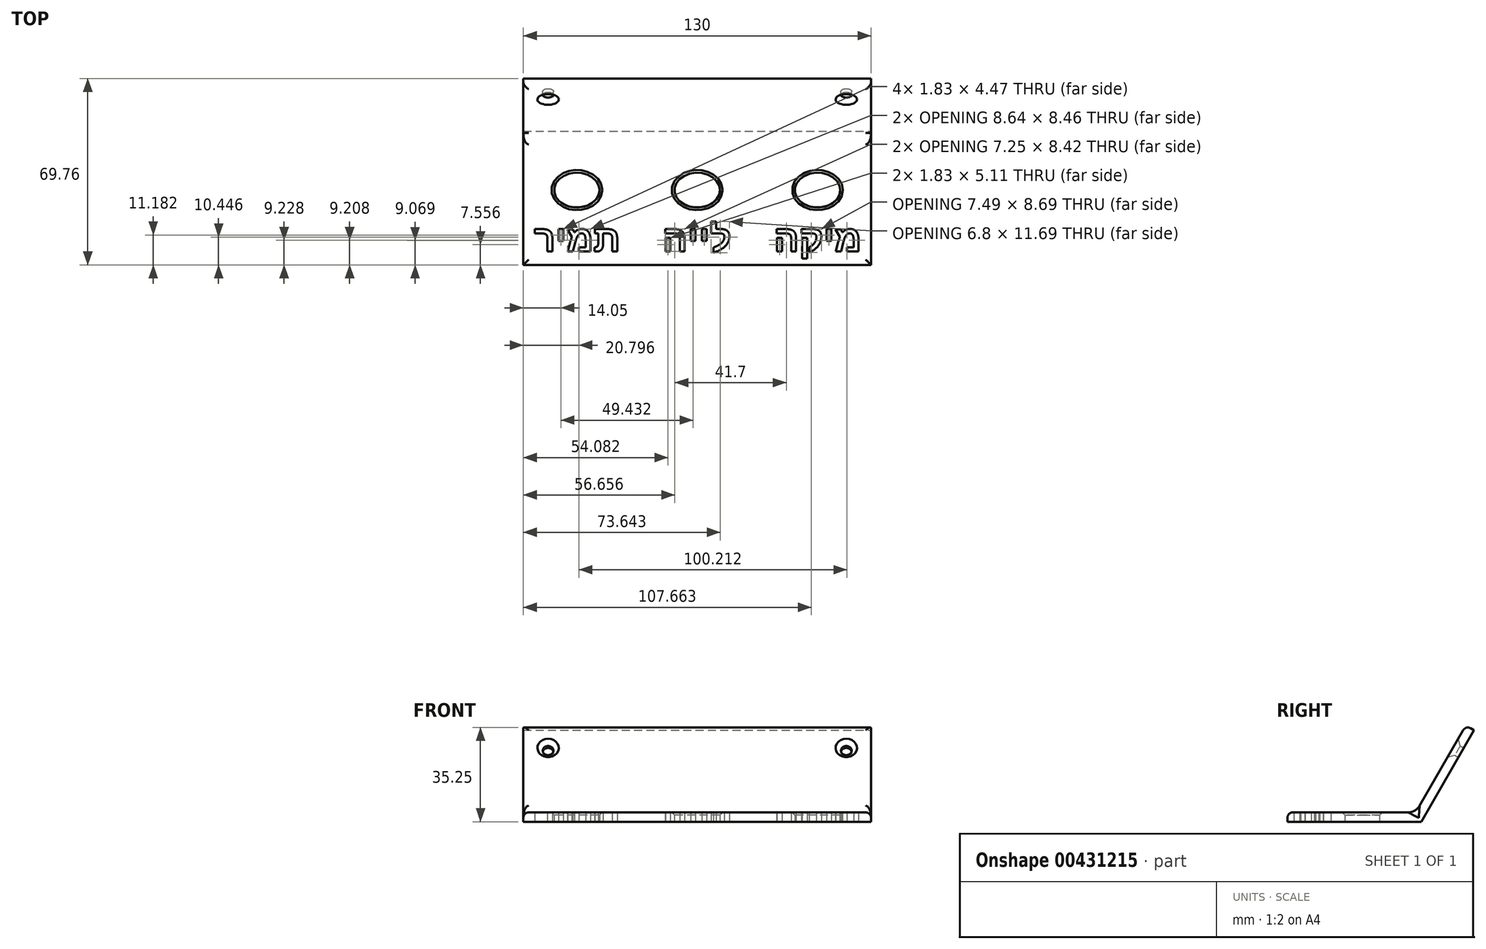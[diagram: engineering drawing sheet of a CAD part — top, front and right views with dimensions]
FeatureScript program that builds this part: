
annotation { "Feature Type Name" : "Feature", "Feature Type Description" : "" }
export const myFeature = defineFeature(function(context is Context, id is Id, definition is map)
    precondition{}
    {
        {
            var Q0;
            Q0=qCreatedBy(makeId("Top.planeOp"),FACE);
            var sketch = newSketch(context, id + "F0", { "sketchPlane" : qUnion([Q0])});
            skLineSegment(sketch, "E0.bottom", {"start": v(-65, 0) * mm, "end": v(65, 0) * mm});
            skLineSegment(sketch, "E0.top", {"start": v(-65, -50) * mm, "end": v(65, -50) * mm});
            skLineSegment(sketch, "E0.left", {"start": v(-65, 0) * mm, "end": v(-65, -50) * mm});
            skLineSegment(sketch, "E0.right", {"start": v(65, 0) * mm, "end": v(65, -50) * mm});
            skText(sketch, "E1", { "text": "רימת", "fontName": "Arimo-Bold.ttf"});
            skText(sketch, "E2", { "text": "הייל", "fontName": "Arimo-Bold.ttf"});
            skText(sketch, "E3", { "text": "הקימ", "fontName": "Arimo-Bold.ttf"});
            skLineSegment(sketch, "E4", {"start": v(0, 0) * mm, "end": v(0, -45) * mm});
            skLineSegment(sketch, "E5", {"start": v(-65, -22) * mm, "end": v(65, -22) * mm, "construction": true});
            skPoint(sketch, "E6", {"position": v(0, 0) * mm});
            skLineSegment(sketch, "E7", {"start": v(-65, -45) * mm, "end": v(65, -45) * mm, "construction": true});
            skEllipse(sketch, "E8", {"center": v(-45, -22) * mm, "majorRadius": 8.5 * mm, "minorRadius": 6.5 * mm, "majorAxis": v(1, 0)});
            skEllipse(sketch, "E9", {"center": v(45, -22) * mm, "majorRadius": 8.5 * mm, "minorRadius": 6.5 * mm, "majorAxis": v(1, 0)});
            skEllipse(sketch, "E10", {"center": v(0, -22) * mm, "majorRadius": 8.5 * mm, "minorRadius": 6.5 * mm, "majorAxis": v(1, 0)});
            const initialGuessF0  = {"E1": [-0.06105, -0.045, 1, 0, 0.01], "E2": [-0.013, -0.045, 1, 0, 0.01], "E3": [0.0287, -0.045, 1, 0, 0.01]};
            skSetInitialGuess(sketch, initialGuessF0);
            skSolve(sketch);
        }
        {
            var Q0;
            Q0=makeQuery(id+"F0.imprint","IMPRINT",FACE,{"disambiguationData":[TD([[makeQuery(id+"F0.imprint","IMPRINT",EDGE,{"derivedFrom":sQuery(id+"F0.wireOp",EDGE,"E0.bottom")}),-1.0]])]});
            extrude(context, id + "F1", {"entities" : qUnion([Q0]), "depth" : 3.5 * mm});
        }
        {
            var Q0;
            Q0=makeQuery(id+"F1.opExtrude","CAP_EDGE",EDGE,{"disambiguationData":[OSD([sQuery(id+"F0.wireOp",EDGE,"E8")])],"isStart":false});
            var Q1;
            Q1=makeQuery(id+"F1.opExtrude","CAP_EDGE",EDGE,{"disambiguationData":[OSD([sQuery(id+"F0.wireOp",EDGE,"E10")])],"isStart":false});
            var Q2;
            Q2=makeQuery(id+"F1.opExtrude","CAP_EDGE",EDGE,{"disambiguationData":[OSD([sQuery(id+"F0.wireOp",EDGE,"E9")])],"isStart":false});
            chamfer(context, id + "F2", {"entities" : qUnion([Q0, Q1, Q2]), "width" : 1 * mm, "tangentPropagation" : true});
        }
        {
            var Q0;
            Q0=makeQuery(id+"F1.opExtrude","CAP_EDGE",EDGE,{"disambiguationData":[OSD([sQuery(id+"F0.wireOp",EDGE,"E0.bottom")])],"isStart":true});
            cPlane(context, id + "F3", {"entities" : qUnion([Q0]), "cplaneType" : CPlaneType.LINE_ANGLE, "offset" : 25 * mm, "angle" : 330 * degree, "width" : 150 * mm, "height" : 150 * mm});
        }
        {
            var Q0;
            Q0=qCreatedBy(id+"F3.planeOp",FACE);
            var sketch = newSketch(context, id + "F4", { "sketchPlane" : qUnion([Q0])});
            skLineSegment(sketch, "E11.bottom", {"start": v(65, 0) * mm, "end": v(-65, 0) * mm});
            skLineSegment(sketch, "E11.top", {"start": v(65, 0) * mm, "end": v(-65, 0) * mm});
            skLineSegment(sketch, "E11.left", {"start": v(65, 0) * mm, "end": v(65, 0) * mm});
            skLineSegment(sketch, "E11.right", {"start": v(-65, 0) * mm, "end": v(-65, 0) * mm});
            skLineSegment(sketch, "E12.bottom", {"start": v(65, 39.53) * mm, "end": v(-65, 39.53) * mm});
            skLineSegment(sketch, "E12.left", {"start": v(65, 39.53) * mm, "end": v(65, 0) * mm});
            skLineSegment(sketch, "E12.right", {"start": v(-65, 39.53) * mm, "end": v(-65, 0) * mm});
            skPoint(sketch, "E13", {"position": v(0, 0) * mm});
            skPoint(sketch, "E14", {"position": v(0, 39.53) * mm});
            skLineSegment(sketch, "E15", {"start": v(0, 39.53) * mm, "end": v(0, 0) * mm, "construction": true});
            skCircle(sketch, "E16", {"center": v(-55.75, 29.86) * mm, "radius": 2 * mm});
            skCircle(sketch, "E17.MirrorC", {"center": v(55.75, 29.86) * mm, "radius": 2 * mm});
            skSolve(sketch);
        }
        {
            var Q0;
            Q0 = qSketchRegion(id + "F4", true);
            extrude(context, id + "F5", {"entities" : qUnion([Q0]), "operationType" : NewBodyOperationType.ADD, "oppositeDirection" : true, "depth" : 3.5 * mm});
        }
        {
            var Q0;
            Q0=makeQuery(id+"F1.opExtrude","CAP_EDGE",EDGE,{"disambiguationData":[OSD([sQuery(id+"F0.wireOp",EDGE,"E0.left")])],"isStart":false});
            var Q1;
            Q1=makeQuery(id+"F1.opExtrude","CAP_EDGE",EDGE,{"disambiguationData":[OSD([sQuery(id+"F0.wireOp",EDGE,"E0.top")])],"isStart":false});
            var Q2;
            Q2=makeQuery(id+"F1.opExtrude","CAP_EDGE",EDGE,{"disambiguationData":[OSD([sQuery(id+"F0.wireOp",EDGE,"E0.right")])],"isStart":false});
            var Q3;
            {var subQ0=sQuery(id+"F4.wireOp",EDGE,"E12.left");var subQ1=sQuery(id+"F0.wireOp",EDGE,"E0.right");Q3=makeQuery(id+"FBdAfcJwTmfcVVD_1.opChamfer","BLEND_EDGE",EDGE,{"blendedFrom":[makeQuery(id+"F5.boolean.opBoolean","INTERSECT",EDGE,{"derivedFrom":[makeQuery(id+"F1.opExtrude","CAP_FACE",FACE,{"disambiguationData":[OSD([sQuery(id+"F0.wireOp",EDGE,"E0.bottom"),sQuery(id+"F0.wireOp",EDGE,"E0.top"),sQuery(id+"F0.wireOp",EDGE,"E0.left"),subQ1,sQuery(id+"F0.wireOp",EDGE,"E1.sketch_text.stroke-0"),sQuery(id+"F0.wireOp",EDGE,"E1.sketch_text.stroke-1"),sQuery(id+"F0.wireOp",EDGE,"E1.sketch_text.stroke-2"),sQuery(id+"F0.wireOp",EDGE,"E1.sketch_text.stroke-3"),sQuery(id+"F0.wireOp",EDGE,"E1.sketch_text.stroke-4"),sQuery(id+"F0.wireOp",EDGE,"E1.sketch_text.stroke-5"),sQuery(id+"F0.wireOp",EDGE,"E1.sketch_text.stroke-6"),sQuery(id+"F0.wireOp",EDGE,"E1.sketch_text.stroke-7"),sQuery(id+"F0.wireOp",EDGE,"E1.sketch_text.stroke-8"),sQuery(id+"F0.wireOp",EDGE,"E1.sketch_text.stroke-9"),sQuery(id+"F0.wireOp",EDGE,"E1.sketch_text.stroke-10"),sQuery(id+"F0.wireOp",EDGE,"E1.sketch_text.stroke-11"),sQuery(id+"F0.wireOp",EDGE,"E1.sketch_text.stroke-12"),sQuery(id+"F0.wireOp",EDGE,"E1.sketch_text.stroke-13"),sQuery(id+"F0.wireOp",EDGE,"E1.sketch_text.stroke-14"),sQuery(id+"F0.wireOp",EDGE,"E1.sketch_text.stroke-15"),sQuery(id+"F0.wireOp",EDGE,"E1.sketch_text.stroke-16"),sQuery(id+"F0.wireOp",EDGE,"E1.sketch_text.stroke-17"),sQuery(id+"F0.wireOp",EDGE,"E1.sketch_text.stroke-18"),sQuery(id+"F0.wireOp",EDGE,"E1.sketch_text.stroke-19"),sQuery(id+"F0.wireOp",EDGE,"E1.sketch_text.stroke-20"),sQuery(id+"F0.wireOp",EDGE,"E1.sketch_text.stroke-21"),sQuery(id+"F0.wireOp",EDGE,"E1.sketch_text.stroke-22"),sQuery(id+"F0.wireOp",EDGE,"E1.sketch_text.stroke-23"),sQuery(id+"F0.wireOp",EDGE,"E1.sketch_text.stroke-24"),sQuery(id+"F0.wireOp",EDGE,"E1.sketch_text.stroke-25"),sQuery(id+"F0.wireOp",EDGE,"E1.sketch_text.stroke-26"),sQuery(id+"F0.wireOp",EDGE,"E1.sketch_text.stroke-27"),sQuery(id+"F0.wireOp",EDGE,"E1.sketch_text.stroke-28"),sQuery(id+"F0.wireOp",EDGE,"E1.sketch_text.stroke-29"),sQuery(id+"F0.wireOp",EDGE,"E1.sketch_text.stroke-30"),sQuery(id+"F0.wireOp",EDGE,"E1.sketch_text.stroke-31"),sQuery(id+"F0.wireOp",EDGE,"E1.sketch_text.stroke-32"),sQuery(id+"F0.wireOp",EDGE,"E1.sketch_text.stroke-33"),sQuery(id+"F0.wireOp",EDGE,"E1.sketch_text.stroke-34"),sQuery(id+"F0.wireOp",EDGE,"E1.sketch_text.stroke-35"),sQuery(id+"F0.wireOp",EDGE,"E1.sketch_text.stroke-36"),sQuery(id+"F0.wireOp",EDGE,"E1.sketch_text.stroke-37"),sQuery(id+"F0.wireOp",EDGE,"E1.sketch_text.stroke-38"),sQuery(id+"F0.wireOp",EDGE,"E1.sketch_text.stroke-39"),sQuery(id+"F0.wireOp",EDGE,"E1.sketch_text.stroke-40"),sQuery(id+"F0.wireOp",EDGE,"E1.sketch_text.stroke-41"),sQuery(id+"F0.wireOp",EDGE,"E1.sketch_text.stroke-42"),sQuery(id+"F0.wireOp",EDGE,"E1.sketch_text.stroke-43"),sQuery(id+"F0.wireOp",EDGE,"E1.sketch_text.stroke-44"),sQuery(id+"F0.wireOp",EDGE,"E1.sketch_text.stroke-45"),sQuery(id+"F0.wireOp",EDGE,"E1.sketch_text.stroke-46"),sQuery(id+"F0.wireOp",EDGE,"E1.sketch_text.stroke-47"),sQuery(id+"F0.wireOp",EDGE,"E1.sketch_text.stroke-48"),sQuery(id+"F0.wireOp",EDGE,"E1.sketch_text.stroke-49"),sQuery(id+"F0.wireOp",EDGE,"E1.sketch_text.stroke-50"),sQuery(id+"F0.wireOp",EDGE,"E1.sketch_text.stroke-51"),sQuery(id+"F0.wireOp",EDGE,"E1.sketch_text.stroke-52"),sQuery(id+"F0.wireOp",EDGE,"E1.sketch_text.stroke-53"),sQuery(id+"F0.wireOp",EDGE,"E1.sketch_text.stroke-54"),sQuery(id+"F0.wireOp",EDGE,"E1.sketch_text.stroke-55"),sQuery(id+"F0.wireOp",EDGE,"E2.sketch_text.stroke-0"),sQuery(id+"F0.wireOp",EDGE,"E2.sketch_text.stroke-1"),sQuery(id+"F0.wireOp",EDGE,"E2.sketch_text.stroke-2"),sQuery(id+"F0.wireOp",EDGE,"E2.sketch_text.stroke-3"),sQuery(id+"F0.wireOp",EDGE,"E2.sketch_text.stroke-4"),sQuery(id+"F0.wireOp",EDGE,"E2.sketch_text.stroke-5"),sQuery(id+"F0.wireOp",EDGE,"E2.sketch_text.stroke-6"),sQuery(id+"F0.wireOp",EDGE,"E2.sketch_text.stroke-7"),sQuery(id+"F0.wireOp",EDGE,"E2.sketch_text.stroke-8"),sQuery(id+"F0.wireOp",EDGE,"E2.sketch_text.stroke-9"),sQuery(id+"F0.wireOp",EDGE,"E2.sketch_text.stroke-10"),sQuery(id+"F0.wireOp",EDGE,"E2.sketch_text.stroke-11"),sQuery(id+"F0.wireOp",EDGE,"E2.sketch_text.stroke-12"),sQuery(id+"F0.wireOp",EDGE,"E2.sketch_text.stroke-13"),sQuery(id+"F0.wireOp",EDGE,"E2.sketch_text.stroke-14"),sQuery(id+"F0.wireOp",EDGE,"E2.sketch_text.stroke-15"),sQuery(id+"F0.wireOp",EDGE,"E2.sketch_text.stroke-16"),sQuery(id+"F0.wireOp",EDGE,"E2.sketch_text.stroke-17"),sQuery(id+"F0.wireOp",EDGE,"E2.sketch_text.stroke-18"),sQuery(id+"F0.wireOp",EDGE,"E2.sketch_text.stroke-19"),sQuery(id+"F0.wireOp",EDGE,"E2.sketch_text.stroke-20"),sQuery(id+"F0.wireOp",EDGE,"E2.sketch_text.stroke-21"),sQuery(id+"F0.wireOp",EDGE,"E2.sketch_text.stroke-22"),sQuery(id+"F0.wireOp",EDGE,"E2.sketch_text.stroke-23"),sQuery(id+"F0.wireOp",EDGE,"E2.sketch_text.stroke-24"),sQuery(id+"F0.wireOp",EDGE,"E2.sketch_text.stroke-25"),sQuery(id+"F0.wireOp",EDGE,"E2.sketch_text.stroke-26"),sQuery(id+"F0.wireOp",EDGE,"E2.sketch_text.stroke-27"),sQuery(id+"F0.wireOp",EDGE,"E2.sketch_text.stroke-28"),sQuery(id+"F0.wireOp",EDGE,"E2.sketch_text.stroke-29"),sQuery(id+"F0.wireOp",EDGE,"E2.sketch_text.stroke-30"),sQuery(id+"F0.wireOp",EDGE,"E2.sketch_text.stroke-31"),sQuery(id+"F0.wireOp",EDGE,"E2.sketch_text.stroke-32"),sQuery(id+"F0.wireOp",EDGE,"E2.sketch_text.stroke-33"),sQuery(id+"F0.wireOp",EDGE,"E3.sketch_text.stroke-0"),sQuery(id+"F0.wireOp",EDGE,"E3.sketch_text.stroke-1"),sQuery(id+"F0.wireOp",EDGE,"E3.sketch_text.stroke-2"),sQuery(id+"F0.wireOp",EDGE,"E3.sketch_text.stroke-3"),sQuery(id+"F0.wireOp",EDGE,"E3.sketch_text.stroke-4"),sQuery(id+"F0.wireOp",EDGE,"E3.sketch_text.stroke-5"),sQuery(id+"F0.wireOp",EDGE,"E3.sketch_text.stroke-6"),sQuery(id+"F0.wireOp",EDGE,"E3.sketch_text.stroke-7"),sQuery(id+"F0.wireOp",EDGE,"E3.sketch_text.stroke-8"),sQuery(id+"F0.wireOp",EDGE,"E3.sketch_text.stroke-9"),sQuery(id+"F0.wireOp",EDGE,"E3.sketch_text.stroke-10"),sQuery(id+"F0.wireOp",EDGE,"E3.sketch_text.stroke-11"),sQuery(id+"F0.wireOp",EDGE,"E3.sketch_text.stroke-12"),sQuery(id+"F0.wireOp",EDGE,"E3.sketch_text.stroke-13"),sQuery(id+"F0.wireOp",EDGE,"E3.sketch_text.stroke-14"),sQuery(id+"F0.wireOp",EDGE,"E3.sketch_text.stroke-15"),sQuery(id+"F0.wireOp",EDGE,"E3.sketch_text.stroke-16"),sQuery(id+"F0.wireOp",EDGE,"E3.sketch_text.stroke-17"),sQuery(id+"F0.wireOp",EDGE,"E3.sketch_text.stroke-18"),sQuery(id+"F0.wireOp",EDGE,"E3.sketch_text.stroke-19"),sQuery(id+"F0.wireOp",EDGE,"E3.sketch_text.stroke-20"),sQuery(id+"F0.wireOp",EDGE,"E3.sketch_text.stroke-21"),sQuery(id+"F0.wireOp",EDGE,"E3.sketch_text.stroke-22"),sQuery(id+"F0.wireOp",EDGE,"E3.sketch_text.stroke-23"),sQuery(id+"F0.wireOp",EDGE,"E3.sketch_text.stroke-24"),sQuery(id+"F0.wireOp",EDGE,"E3.sketch_text.stroke-25"),sQuery(id+"F0.wireOp",EDGE,"E3.sketch_text.stroke-26"),sQuery(id+"F0.wireOp",EDGE,"E3.sketch_text.stroke-27"),sQuery(id+"F0.wireOp",EDGE,"E3.sketch_text.stroke-28"),sQuery(id+"F0.wireOp",EDGE,"E3.sketch_text.stroke-29"),sQuery(id+"F0.wireOp",EDGE,"E3.sketch_text.stroke-30"),sQuery(id+"F0.wireOp",EDGE,"E3.sketch_text.stroke-31"),sQuery(id+"F0.wireOp",EDGE,"E3.sketch_text.stroke-32"),sQuery(id+"F0.wireOp",EDGE,"E3.sketch_text.stroke-33"),sQuery(id+"F0.wireOp",EDGE,"E3.sketch_text.stroke-34"),sQuery(id+"F0.wireOp",EDGE,"E3.sketch_text.stroke-35"),sQuery(id+"F0.wireOp",EDGE,"E3.sketch_text.stroke-36"),sQuery(id+"F0.wireOp",EDGE,"E3.sketch_text.stroke-37"),sQuery(id+"F0.wireOp",EDGE,"E3.sketch_text.stroke-38"),sQuery(id+"F0.wireOp",EDGE,"E3.sketch_text.stroke-39"),sQuery(id+"F0.wireOp",EDGE,"E3.sketch_text.stroke-40"),sQuery(id+"F0.wireOp",EDGE,"E3.sketch_text.stroke-41"),sQuery(id+"F0.wireOp",EDGE,"E3.sketch_text.stroke-42"),sQuery(id+"F0.wireOp",EDGE,"E3.sketch_text.stroke-43"),sQuery(id+"F0.wireOp",EDGE,"E3.sketch_text.stroke-44"),sQuery(id+"F0.wireOp",EDGE,"E3.sketch_text.stroke-45"),sQuery(id+"F0.wireOp",EDGE,"E3.sketch_text.stroke-46"),sQuery(id+"F0.wireOp",EDGE,"E3.sketch_text.stroke-47"),sQuery(id+"F0.wireOp",EDGE,"E3.sketch_text.stroke-48"),sQuery(id+"F0.wireOp",EDGE,"E3.sketch_text.stroke-49"),sQuery(id+"F0.wireOp",EDGE,"E3.sketch_text.stroke-50"),sQuery(id+"F0.wireOp",EDGE,"E3.sketch_text.stroke-51"),sQuery(id+"F0.wireOp",EDGE,"E3.sketch_text.stroke-52"),sQuery(id+"F0.wireOp",EDGE,"E3.sketch_text.stroke-53"),sQuery(id+"F0.wireOp",EDGE,"E8"),sQuery(id+"F0.wireOp",EDGE,"E9"),sQuery(id+"F0.wireOp",EDGE,"E10")])],"isStart":false}),makeQuery(id+"F5.opExtrude","CAP_FACE",FACE,{"disambiguationData":[OSD([sQuery(id+"F4.wireOp",EDGE,"E12.bottom"),sQuery(id+"F4.wireOp",EDGE,"E11.bottom"),subQ0,sQuery(id+"F4.wireOp",EDGE,"E12.right")])],"isStart":false})]}),makeQuery(id+"F5.boolean.opBoolean","MERGE",FACE,{"derivedFrom":[makeQuery(id+"F1.opExtrude","SWEPT_FACE",FACE,{"disambiguationData":[OSD([subQ1])]}),makeQuery(id+"F5.opExtrude","SWEPT_FACE",FACE,{"disambiguationData":[OSD([subQ0])]})]})],"blendedInto":[makeQuery(id+"F5.boolean.opBoolean","MERGE",FACE,{"derivedFrom":[makeQuery(id+"F1.opExtrude","SWEPT_FACE",FACE,{"disambiguationData":[OSD([subQ1])]}),makeQuery(id+"F5.opExtrude","SWEPT_FACE",FACE,{"disambiguationData":[OSD([subQ0])]})]})]});}
            var Q4;
            Q4=makeQuery(id+"F5.opExtrude","CAP_EDGE",EDGE,{"disambiguationData":[OSD([sQuery(id+"F4.wireOp",EDGE,"E12.left")])],"isStart":false});
            var Q5;
            Q5=makeQuery(id+"F5.opExtrude","CAP_EDGE",EDGE,{"disambiguationData":[OSD([sQuery(id+"F4.wireOp",EDGE,"E12.bottom")])],"isStart":false});
            var Q6;
            Q6=makeQuery(id+"F5.opExtrude","CAP_EDGE",EDGE,{"disambiguationData":[OSD([sQuery(id+"F4.wireOp",EDGE,"E12.right")])],"isStart":false});
            var Q7;
            {var subQ0=sQuery(id+"F4.wireOp",EDGE,"E12.right");var subQ1=sQuery(id+"F0.wireOp",EDGE,"E0.left");Q7=makeQuery(id+"FBdAfcJwTmfcVVD_1.opChamfer","BLEND_EDGE",EDGE,{"blendedFrom":[makeQuery(id+"F5.boolean.opBoolean","INTERSECT",EDGE,{"derivedFrom":[makeQuery(id+"F1.opExtrude","CAP_FACE",FACE,{"disambiguationData":[OSD([sQuery(id+"F0.wireOp",EDGE,"E0.bottom"),sQuery(id+"F0.wireOp",EDGE,"E0.top"),subQ1,sQuery(id+"F0.wireOp",EDGE,"E0.right"),sQuery(id+"F0.wireOp",EDGE,"E1.sketch_text.stroke-0"),sQuery(id+"F0.wireOp",EDGE,"E1.sketch_text.stroke-1"),sQuery(id+"F0.wireOp",EDGE,"E1.sketch_text.stroke-2"),sQuery(id+"F0.wireOp",EDGE,"E1.sketch_text.stroke-3"),sQuery(id+"F0.wireOp",EDGE,"E1.sketch_text.stroke-4"),sQuery(id+"F0.wireOp",EDGE,"E1.sketch_text.stroke-5"),sQuery(id+"F0.wireOp",EDGE,"E1.sketch_text.stroke-6"),sQuery(id+"F0.wireOp",EDGE,"E1.sketch_text.stroke-7"),sQuery(id+"F0.wireOp",EDGE,"E1.sketch_text.stroke-8"),sQuery(id+"F0.wireOp",EDGE,"E1.sketch_text.stroke-9"),sQuery(id+"F0.wireOp",EDGE,"E1.sketch_text.stroke-10"),sQuery(id+"F0.wireOp",EDGE,"E1.sketch_text.stroke-11"),sQuery(id+"F0.wireOp",EDGE,"E1.sketch_text.stroke-12"),sQuery(id+"F0.wireOp",EDGE,"E1.sketch_text.stroke-13"),sQuery(id+"F0.wireOp",EDGE,"E1.sketch_text.stroke-14"),sQuery(id+"F0.wireOp",EDGE,"E1.sketch_text.stroke-15"),sQuery(id+"F0.wireOp",EDGE,"E1.sketch_text.stroke-16"),sQuery(id+"F0.wireOp",EDGE,"E1.sketch_text.stroke-17"),sQuery(id+"F0.wireOp",EDGE,"E1.sketch_text.stroke-18"),sQuery(id+"F0.wireOp",EDGE,"E1.sketch_text.stroke-19"),sQuery(id+"F0.wireOp",EDGE,"E1.sketch_text.stroke-20"),sQuery(id+"F0.wireOp",EDGE,"E1.sketch_text.stroke-21"),sQuery(id+"F0.wireOp",EDGE,"E1.sketch_text.stroke-22"),sQuery(id+"F0.wireOp",EDGE,"E1.sketch_text.stroke-23"),sQuery(id+"F0.wireOp",EDGE,"E1.sketch_text.stroke-24"),sQuery(id+"F0.wireOp",EDGE,"E1.sketch_text.stroke-25"),sQuery(id+"F0.wireOp",EDGE,"E1.sketch_text.stroke-26"),sQuery(id+"F0.wireOp",EDGE,"E1.sketch_text.stroke-27"),sQuery(id+"F0.wireOp",EDGE,"E1.sketch_text.stroke-28"),sQuery(id+"F0.wireOp",EDGE,"E1.sketch_text.stroke-29"),sQuery(id+"F0.wireOp",EDGE,"E1.sketch_text.stroke-30"),sQuery(id+"F0.wireOp",EDGE,"E1.sketch_text.stroke-31"),sQuery(id+"F0.wireOp",EDGE,"E1.sketch_text.stroke-32"),sQuery(id+"F0.wireOp",EDGE,"E1.sketch_text.stroke-33"),sQuery(id+"F0.wireOp",EDGE,"E1.sketch_text.stroke-34"),sQuery(id+"F0.wireOp",EDGE,"E1.sketch_text.stroke-35"),sQuery(id+"F0.wireOp",EDGE,"E1.sketch_text.stroke-36"),sQuery(id+"F0.wireOp",EDGE,"E1.sketch_text.stroke-37"),sQuery(id+"F0.wireOp",EDGE,"E1.sketch_text.stroke-38"),sQuery(id+"F0.wireOp",EDGE,"E1.sketch_text.stroke-39"),sQuery(id+"F0.wireOp",EDGE,"E1.sketch_text.stroke-40"),sQuery(id+"F0.wireOp",EDGE,"E1.sketch_text.stroke-41"),sQuery(id+"F0.wireOp",EDGE,"E1.sketch_text.stroke-42"),sQuery(id+"F0.wireOp",EDGE,"E1.sketch_text.stroke-43"),sQuery(id+"F0.wireOp",EDGE,"E1.sketch_text.stroke-44"),sQuery(id+"F0.wireOp",EDGE,"E1.sketch_text.stroke-45"),sQuery(id+"F0.wireOp",EDGE,"E1.sketch_text.stroke-46"),sQuery(id+"F0.wireOp",EDGE,"E1.sketch_text.stroke-47"),sQuery(id+"F0.wireOp",EDGE,"E1.sketch_text.stroke-48"),sQuery(id+"F0.wireOp",EDGE,"E1.sketch_text.stroke-49"),sQuery(id+"F0.wireOp",EDGE,"E1.sketch_text.stroke-50"),sQuery(id+"F0.wireOp",EDGE,"E1.sketch_text.stroke-51"),sQuery(id+"F0.wireOp",EDGE,"E1.sketch_text.stroke-52"),sQuery(id+"F0.wireOp",EDGE,"E1.sketch_text.stroke-53"),sQuery(id+"F0.wireOp",EDGE,"E1.sketch_text.stroke-54"),sQuery(id+"F0.wireOp",EDGE,"E1.sketch_text.stroke-55"),sQuery(id+"F0.wireOp",EDGE,"E2.sketch_text.stroke-0"),sQuery(id+"F0.wireOp",EDGE,"E2.sketch_text.stroke-1"),sQuery(id+"F0.wireOp",EDGE,"E2.sketch_text.stroke-2"),sQuery(id+"F0.wireOp",EDGE,"E2.sketch_text.stroke-3"),sQuery(id+"F0.wireOp",EDGE,"E2.sketch_text.stroke-4"),sQuery(id+"F0.wireOp",EDGE,"E2.sketch_text.stroke-5"),sQuery(id+"F0.wireOp",EDGE,"E2.sketch_text.stroke-6"),sQuery(id+"F0.wireOp",EDGE,"E2.sketch_text.stroke-7"),sQuery(id+"F0.wireOp",EDGE,"E2.sketch_text.stroke-8"),sQuery(id+"F0.wireOp",EDGE,"E2.sketch_text.stroke-9"),sQuery(id+"F0.wireOp",EDGE,"E2.sketch_text.stroke-10"),sQuery(id+"F0.wireOp",EDGE,"E2.sketch_text.stroke-11"),sQuery(id+"F0.wireOp",EDGE,"E2.sketch_text.stroke-12"),sQuery(id+"F0.wireOp",EDGE,"E2.sketch_text.stroke-13"),sQuery(id+"F0.wireOp",EDGE,"E2.sketch_text.stroke-14"),sQuery(id+"F0.wireOp",EDGE,"E2.sketch_text.stroke-15"),sQuery(id+"F0.wireOp",EDGE,"E2.sketch_text.stroke-16"),sQuery(id+"F0.wireOp",EDGE,"E2.sketch_text.stroke-17"),sQuery(id+"F0.wireOp",EDGE,"E2.sketch_text.stroke-18"),sQuery(id+"F0.wireOp",EDGE,"E2.sketch_text.stroke-19"),sQuery(id+"F0.wireOp",EDGE,"E2.sketch_text.stroke-20"),sQuery(id+"F0.wireOp",EDGE,"E2.sketch_text.stroke-21"),sQuery(id+"F0.wireOp",EDGE,"E2.sketch_text.stroke-22"),sQuery(id+"F0.wireOp",EDGE,"E2.sketch_text.stroke-23"),sQuery(id+"F0.wireOp",EDGE,"E2.sketch_text.stroke-24"),sQuery(id+"F0.wireOp",EDGE,"E2.sketch_text.stroke-25"),sQuery(id+"F0.wireOp",EDGE,"E2.sketch_text.stroke-26"),sQuery(id+"F0.wireOp",EDGE,"E2.sketch_text.stroke-27"),sQuery(id+"F0.wireOp",EDGE,"E2.sketch_text.stroke-28"),sQuery(id+"F0.wireOp",EDGE,"E2.sketch_text.stroke-29"),sQuery(id+"F0.wireOp",EDGE,"E2.sketch_text.stroke-30"),sQuery(id+"F0.wireOp",EDGE,"E2.sketch_text.stroke-31"),sQuery(id+"F0.wireOp",EDGE,"E2.sketch_text.stroke-32"),sQuery(id+"F0.wireOp",EDGE,"E2.sketch_text.stroke-33"),sQuery(id+"F0.wireOp",EDGE,"E3.sketch_text.stroke-0"),sQuery(id+"F0.wireOp",EDGE,"E3.sketch_text.stroke-1"),sQuery(id+"F0.wireOp",EDGE,"E3.sketch_text.stroke-2"),sQuery(id+"F0.wireOp",EDGE,"E3.sketch_text.stroke-3"),sQuery(id+"F0.wireOp",EDGE,"E3.sketch_text.stroke-4"),sQuery(id+"F0.wireOp",EDGE,"E3.sketch_text.stroke-5"),sQuery(id+"F0.wireOp",EDGE,"E3.sketch_text.stroke-6"),sQuery(id+"F0.wireOp",EDGE,"E3.sketch_text.stroke-7"),sQuery(id+"F0.wireOp",EDGE,"E3.sketch_text.stroke-8"),sQuery(id+"F0.wireOp",EDGE,"E3.sketch_text.stroke-9"),sQuery(id+"F0.wireOp",EDGE,"E3.sketch_text.stroke-10"),sQuery(id+"F0.wireOp",EDGE,"E3.sketch_text.stroke-11"),sQuery(id+"F0.wireOp",EDGE,"E3.sketch_text.stroke-12"),sQuery(id+"F0.wireOp",EDGE,"E3.sketch_text.stroke-13"),sQuery(id+"F0.wireOp",EDGE,"E3.sketch_text.stroke-14"),sQuery(id+"F0.wireOp",EDGE,"E3.sketch_text.stroke-15"),sQuery(id+"F0.wireOp",EDGE,"E3.sketch_text.stroke-16"),sQuery(id+"F0.wireOp",EDGE,"E3.sketch_text.stroke-17"),sQuery(id+"F0.wireOp",EDGE,"E3.sketch_text.stroke-18"),sQuery(id+"F0.wireOp",EDGE,"E3.sketch_text.stroke-19"),sQuery(id+"F0.wireOp",EDGE,"E3.sketch_text.stroke-20"),sQuery(id+"F0.wireOp",EDGE,"E3.sketch_text.stroke-21"),sQuery(id+"F0.wireOp",EDGE,"E3.sketch_text.stroke-22"),sQuery(id+"F0.wireOp",EDGE,"E3.sketch_text.stroke-23"),sQuery(id+"F0.wireOp",EDGE,"E3.sketch_text.stroke-24"),sQuery(id+"F0.wireOp",EDGE,"E3.sketch_text.stroke-25"),sQuery(id+"F0.wireOp",EDGE,"E3.sketch_text.stroke-26"),sQuery(id+"F0.wireOp",EDGE,"E3.sketch_text.stroke-27"),sQuery(id+"F0.wireOp",EDGE,"E3.sketch_text.stroke-28"),sQuery(id+"F0.wireOp",EDGE,"E3.sketch_text.stroke-29"),sQuery(id+"F0.wireOp",EDGE,"E3.sketch_text.stroke-30"),sQuery(id+"F0.wireOp",EDGE,"E3.sketch_text.stroke-31"),sQuery(id+"F0.wireOp",EDGE,"E3.sketch_text.stroke-32"),sQuery(id+"F0.wireOp",EDGE,"E3.sketch_text.stroke-33"),sQuery(id+"F0.wireOp",EDGE,"E3.sketch_text.stroke-34"),sQuery(id+"F0.wireOp",EDGE,"E3.sketch_text.stroke-35"),sQuery(id+"F0.wireOp",EDGE,"E3.sketch_text.stroke-36"),sQuery(id+"F0.wireOp",EDGE,"E3.sketch_text.stroke-37"),sQuery(id+"F0.wireOp",EDGE,"E3.sketch_text.stroke-38"),sQuery(id+"F0.wireOp",EDGE,"E3.sketch_text.stroke-39"),sQuery(id+"F0.wireOp",EDGE,"E3.sketch_text.stroke-40"),sQuery(id+"F0.wireOp",EDGE,"E3.sketch_text.stroke-41"),sQuery(id+"F0.wireOp",EDGE,"E3.sketch_text.stroke-42"),sQuery(id+"F0.wireOp",EDGE,"E3.sketch_text.stroke-43"),sQuery(id+"F0.wireOp",EDGE,"E3.sketch_text.stroke-44"),sQuery(id+"F0.wireOp",EDGE,"E3.sketch_text.stroke-45"),sQuery(id+"F0.wireOp",EDGE,"E3.sketch_text.stroke-46"),sQuery(id+"F0.wireOp",EDGE,"E3.sketch_text.stroke-47"),sQuery(id+"F0.wireOp",EDGE,"E3.sketch_text.stroke-48"),sQuery(id+"F0.wireOp",EDGE,"E3.sketch_text.stroke-49"),sQuery(id+"F0.wireOp",EDGE,"E3.sketch_text.stroke-50"),sQuery(id+"F0.wireOp",EDGE,"E3.sketch_text.stroke-51"),sQuery(id+"F0.wireOp",EDGE,"E3.sketch_text.stroke-52"),sQuery(id+"F0.wireOp",EDGE,"E3.sketch_text.stroke-53"),sQuery(id+"F0.wireOp",EDGE,"E8"),sQuery(id+"F0.wireOp",EDGE,"E9"),sQuery(id+"F0.wireOp",EDGE,"E10")])],"isStart":false}),makeQuery(id+"F5.opExtrude","CAP_FACE",FACE,{"disambiguationData":[OSD([sQuery(id+"F4.wireOp",EDGE,"E12.bottom"),sQuery(id+"F4.wireOp",EDGE,"E11.bottom"),sQuery(id+"F4.wireOp",EDGE,"E12.left"),subQ0])],"isStart":false})]}),makeQuery(id+"F5.boolean.opBoolean","MERGE",FACE,{"derivedFrom":[makeQuery(id+"F1.opExtrude","SWEPT_FACE",FACE,{"disambiguationData":[OSD([subQ1])]}),makeQuery(id+"F5.opExtrude","SWEPT_FACE",FACE,{"disambiguationData":[OSD([subQ0])]})]})],"blendedInto":[makeQuery(id+"F5.boolean.opBoolean","MERGE",FACE,{"derivedFrom":[makeQuery(id+"F1.opExtrude","SWEPT_FACE",FACE,{"disambiguationData":[OSD([subQ1])]}),makeQuery(id+"F5.opExtrude","SWEPT_FACE",FACE,{"disambiguationData":[OSD([subQ0])]})]})]});}
            fillet(context, id + "F6", {"entities" : qUnion([Q0, Q1, Q2, Q3, Q4, Q5, Q6, Q7]), "radius" : 2 * mm, "tangentPropagation" : true, "allowEdgeOverflow" : false});
        }
        {
            var Q0;
            Q0=makeQuery(id+"F5.opExtrude","CAP_EDGE",EDGE,{"disambiguationData":[OSD([sQuery(id+"F4.wireOp",EDGE,"E16")])],"isStart":false});
            chamfer(context, id + "F7", {"entities" : qUnion([Q0]), "width" : 2 * mm, "tangentPropagation" : true});
        }
        {
            var Q0;
            Q0=makeQuery(id+"F5.opExtrude","CAP_EDGE",EDGE,{"disambiguationData":[OSD([sQuery(id+"F4.wireOp",EDGE,"E17.MirrorC")])],"isStart":false});
            chamfer(context, id + "F8", {"entities" : qUnion([Q0]), "width" : 2 * mm, "tangentPropagation" : true});
        }
        {
            var Q0;
            Q0=makeQuery(id+"F5.boolean.opBoolean","INTERSECT",EDGE,{"derivedFrom":[makeQuery(id+"F1.opExtrude","CAP_FACE",FACE,{"disambiguationData":[OSD([sQuery(id+"F0.wireOp",EDGE,"E0.bottom"),sQuery(id+"F0.wireOp",EDGE,"E0.top"),sQuery(id+"F0.wireOp",EDGE,"E0.left"),sQuery(id+"F0.wireOp",EDGE,"E0.right"),sQuery(id+"F0.wireOp",EDGE,"E1.sketch_text.stroke-0"),sQuery(id+"F0.wireOp",EDGE,"E1.sketch_text.stroke-1"),sQuery(id+"F0.wireOp",EDGE,"E1.sketch_text.stroke-2"),sQuery(id+"F0.wireOp",EDGE,"E1.sketch_text.stroke-3"),sQuery(id+"F0.wireOp",EDGE,"E1.sketch_text.stroke-4"),sQuery(id+"F0.wireOp",EDGE,"E1.sketch_text.stroke-5"),sQuery(id+"F0.wireOp",EDGE,"E1.sketch_text.stroke-6"),sQuery(id+"F0.wireOp",EDGE,"E1.sketch_text.stroke-7"),sQuery(id+"F0.wireOp",EDGE,"E1.sketch_text.stroke-8"),sQuery(id+"F0.wireOp",EDGE,"E1.sketch_text.stroke-9"),sQuery(id+"F0.wireOp",EDGE,"E1.sketch_text.stroke-10"),sQuery(id+"F0.wireOp",EDGE,"E1.sketch_text.stroke-11"),sQuery(id+"F0.wireOp",EDGE,"E1.sketch_text.stroke-12"),sQuery(id+"F0.wireOp",EDGE,"E1.sketch_text.stroke-13"),sQuery(id+"F0.wireOp",EDGE,"E1.sketch_text.stroke-14"),sQuery(id+"F0.wireOp",EDGE,"E1.sketch_text.stroke-15"),sQuery(id+"F0.wireOp",EDGE,"E1.sketch_text.stroke-16"),sQuery(id+"F0.wireOp",EDGE,"E1.sketch_text.stroke-17"),sQuery(id+"F0.wireOp",EDGE,"E1.sketch_text.stroke-18"),sQuery(id+"F0.wireOp",EDGE,"E1.sketch_text.stroke-19"),sQuery(id+"F0.wireOp",EDGE,"E1.sketch_text.stroke-20"),sQuery(id+"F0.wireOp",EDGE,"E1.sketch_text.stroke-21"),sQuery(id+"F0.wireOp",EDGE,"E1.sketch_text.stroke-22"),sQuery(id+"F0.wireOp",EDGE,"E1.sketch_text.stroke-23"),sQuery(id+"F0.wireOp",EDGE,"E1.sketch_text.stroke-24"),sQuery(id+"F0.wireOp",EDGE,"E1.sketch_text.stroke-25"),sQuery(id+"F0.wireOp",EDGE,"E1.sketch_text.stroke-26"),sQuery(id+"F0.wireOp",EDGE,"E1.sketch_text.stroke-27"),sQuery(id+"F0.wireOp",EDGE,"E1.sketch_text.stroke-28"),sQuery(id+"F0.wireOp",EDGE,"E1.sketch_text.stroke-29"),sQuery(id+"F0.wireOp",EDGE,"E1.sketch_text.stroke-30"),sQuery(id+"F0.wireOp",EDGE,"E1.sketch_text.stroke-31"),sQuery(id+"F0.wireOp",EDGE,"E1.sketch_text.stroke-32"),sQuery(id+"F0.wireOp",EDGE,"E1.sketch_text.stroke-33"),sQuery(id+"F0.wireOp",EDGE,"E1.sketch_text.stroke-34"),sQuery(id+"F0.wireOp",EDGE,"E1.sketch_text.stroke-35"),sQuery(id+"F0.wireOp",EDGE,"E1.sketch_text.stroke-36"),sQuery(id+"F0.wireOp",EDGE,"E1.sketch_text.stroke-37"),sQuery(id+"F0.wireOp",EDGE,"E1.sketch_text.stroke-38"),sQuery(id+"F0.wireOp",EDGE,"E1.sketch_text.stroke-39"),sQuery(id+"F0.wireOp",EDGE,"E1.sketch_text.stroke-40"),sQuery(id+"F0.wireOp",EDGE,"E1.sketch_text.stroke-41"),sQuery(id+"F0.wireOp",EDGE,"E1.sketch_text.stroke-42"),sQuery(id+"F0.wireOp",EDGE,"E1.sketch_text.stroke-43"),sQuery(id+"F0.wireOp",EDGE,"E1.sketch_text.stroke-44"),sQuery(id+"F0.wireOp",EDGE,"E1.sketch_text.stroke-45"),sQuery(id+"F0.wireOp",EDGE,"E1.sketch_text.stroke-46"),sQuery(id+"F0.wireOp",EDGE,"E1.sketch_text.stroke-47"),sQuery(id+"F0.wireOp",EDGE,"E1.sketch_text.stroke-48"),sQuery(id+"F0.wireOp",EDGE,"E1.sketch_text.stroke-49"),sQuery(id+"F0.wireOp",EDGE,"E1.sketch_text.stroke-50"),sQuery(id+"F0.wireOp",EDGE,"E1.sketch_text.stroke-51"),sQuery(id+"F0.wireOp",EDGE,"E1.sketch_text.stroke-52"),sQuery(id+"F0.wireOp",EDGE,"E1.sketch_text.stroke-53"),sQuery(id+"F0.wireOp",EDGE,"E1.sketch_text.stroke-54"),sQuery(id+"F0.wireOp",EDGE,"E1.sketch_text.stroke-55"),sQuery(id+"F0.wireOp",EDGE,"E2.sketch_text.stroke-0"),sQuery(id+"F0.wireOp",EDGE,"E2.sketch_text.stroke-1"),sQuery(id+"F0.wireOp",EDGE,"E2.sketch_text.stroke-2"),sQuery(id+"F0.wireOp",EDGE,"E2.sketch_text.stroke-3"),sQuery(id+"F0.wireOp",EDGE,"E2.sketch_text.stroke-4"),sQuery(id+"F0.wireOp",EDGE,"E2.sketch_text.stroke-5"),sQuery(id+"F0.wireOp",EDGE,"E2.sketch_text.stroke-6"),sQuery(id+"F0.wireOp",EDGE,"E2.sketch_text.stroke-7"),sQuery(id+"F0.wireOp",EDGE,"E2.sketch_text.stroke-8"),sQuery(id+"F0.wireOp",EDGE,"E2.sketch_text.stroke-9"),sQuery(id+"F0.wireOp",EDGE,"E2.sketch_text.stroke-10"),sQuery(id+"F0.wireOp",EDGE,"E2.sketch_text.stroke-11"),sQuery(id+"F0.wireOp",EDGE,"E2.sketch_text.stroke-12"),sQuery(id+"F0.wireOp",EDGE,"E2.sketch_text.stroke-13"),sQuery(id+"F0.wireOp",EDGE,"E2.sketch_text.stroke-14"),sQuery(id+"F0.wireOp",EDGE,"E2.sketch_text.stroke-15"),sQuery(id+"F0.wireOp",EDGE,"E2.sketch_text.stroke-16"),sQuery(id+"F0.wireOp",EDGE,"E2.sketch_text.stroke-17"),sQuery(id+"F0.wireOp",EDGE,"E2.sketch_text.stroke-18"),sQuery(id+"F0.wireOp",EDGE,"E2.sketch_text.stroke-19"),sQuery(id+"F0.wireOp",EDGE,"E2.sketch_text.stroke-20"),sQuery(id+"F0.wireOp",EDGE,"E2.sketch_text.stroke-21"),sQuery(id+"F0.wireOp",EDGE,"E2.sketch_text.stroke-22"),sQuery(id+"F0.wireOp",EDGE,"E2.sketch_text.stroke-23"),sQuery(id+"F0.wireOp",EDGE,"E2.sketch_text.stroke-24"),sQuery(id+"F0.wireOp",EDGE,"E2.sketch_text.stroke-25"),sQuery(id+"F0.wireOp",EDGE,"E2.sketch_text.stroke-26"),sQuery(id+"F0.wireOp",EDGE,"E2.sketch_text.stroke-27"),sQuery(id+"F0.wireOp",EDGE,"E2.sketch_text.stroke-28"),sQuery(id+"F0.wireOp",EDGE,"E2.sketch_text.stroke-29"),sQuery(id+"F0.wireOp",EDGE,"E2.sketch_text.stroke-30"),sQuery(id+"F0.wireOp",EDGE,"E2.sketch_text.stroke-31"),sQuery(id+"F0.wireOp",EDGE,"E2.sketch_text.stroke-32"),sQuery(id+"F0.wireOp",EDGE,"E2.sketch_text.stroke-33"),sQuery(id+"F0.wireOp",EDGE,"E3.sketch_text.stroke-0"),sQuery(id+"F0.wireOp",EDGE,"E3.sketch_text.stroke-1"),sQuery(id+"F0.wireOp",EDGE,"E3.sketch_text.stroke-2"),sQuery(id+"F0.wireOp",EDGE,"E3.sketch_text.stroke-3"),sQuery(id+"F0.wireOp",EDGE,"E3.sketch_text.stroke-4"),sQuery(id+"F0.wireOp",EDGE,"E3.sketch_text.stroke-5"),sQuery(id+"F0.wireOp",EDGE,"E3.sketch_text.stroke-6"),sQuery(id+"F0.wireOp",EDGE,"E3.sketch_text.stroke-7"),sQuery(id+"F0.wireOp",EDGE,"E3.sketch_text.stroke-8"),sQuery(id+"F0.wireOp",EDGE,"E3.sketch_text.stroke-9"),sQuery(id+"F0.wireOp",EDGE,"E3.sketch_text.stroke-10"),sQuery(id+"F0.wireOp",EDGE,"E3.sketch_text.stroke-11"),sQuery(id+"F0.wireOp",EDGE,"E3.sketch_text.stroke-12"),sQuery(id+"F0.wireOp",EDGE,"E3.sketch_text.stroke-13"),sQuery(id+"F0.wireOp",EDGE,"E3.sketch_text.stroke-14"),sQuery(id+"F0.wireOp",EDGE,"E3.sketch_text.stroke-15"),sQuery(id+"F0.wireOp",EDGE,"E3.sketch_text.stroke-16"),sQuery(id+"F0.wireOp",EDGE,"E3.sketch_text.stroke-17"),sQuery(id+"F0.wireOp",EDGE,"E3.sketch_text.stroke-18"),sQuery(id+"F0.wireOp",EDGE,"E3.sketch_text.stroke-19"),sQuery(id+"F0.wireOp",EDGE,"E3.sketch_text.stroke-20"),sQuery(id+"F0.wireOp",EDGE,"E3.sketch_text.stroke-21"),sQuery(id+"F0.wireOp",EDGE,"E3.sketch_text.stroke-22"),sQuery(id+"F0.wireOp",EDGE,"E3.sketch_text.stroke-23"),sQuery(id+"F0.wireOp",EDGE,"E3.sketch_text.stroke-24"),sQuery(id+"F0.wireOp",EDGE,"E3.sketch_text.stroke-25"),sQuery(id+"F0.wireOp",EDGE,"E3.sketch_text.stroke-26"),sQuery(id+"F0.wireOp",EDGE,"E3.sketch_text.stroke-27"),sQuery(id+"F0.wireOp",EDGE,"E3.sketch_text.stroke-28"),sQuery(id+"F0.wireOp",EDGE,"E3.sketch_text.stroke-29"),sQuery(id+"F0.wireOp",EDGE,"E3.sketch_text.stroke-30"),sQuery(id+"F0.wireOp",EDGE,"E3.sketch_text.stroke-31"),sQuery(id+"F0.wireOp",EDGE,"E3.sketch_text.stroke-32"),sQuery(id+"F0.wireOp",EDGE,"E3.sketch_text.stroke-33"),sQuery(id+"F0.wireOp",EDGE,"E3.sketch_text.stroke-34"),sQuery(id+"F0.wireOp",EDGE,"E3.sketch_text.stroke-35"),sQuery(id+"F0.wireOp",EDGE,"E3.sketch_text.stroke-36"),sQuery(id+"F0.wireOp",EDGE,"E3.sketch_text.stroke-37"),sQuery(id+"F0.wireOp",EDGE,"E3.sketch_text.stroke-38"),sQuery(id+"F0.wireOp",EDGE,"E3.sketch_text.stroke-39"),sQuery(id+"F0.wireOp",EDGE,"E3.sketch_text.stroke-40"),sQuery(id+"F0.wireOp",EDGE,"E3.sketch_text.stroke-41"),sQuery(id+"F0.wireOp",EDGE,"E3.sketch_text.stroke-42"),sQuery(id+"F0.wireOp",EDGE,"E3.sketch_text.stroke-43"),sQuery(id+"F0.wireOp",EDGE,"E3.sketch_text.stroke-44"),sQuery(id+"F0.wireOp",EDGE,"E3.sketch_text.stroke-45"),sQuery(id+"F0.wireOp",EDGE,"E3.sketch_text.stroke-46"),sQuery(id+"F0.wireOp",EDGE,"E3.sketch_text.stroke-47"),sQuery(id+"F0.wireOp",EDGE,"E3.sketch_text.stroke-48"),sQuery(id+"F0.wireOp",EDGE,"E3.sketch_text.stroke-49"),sQuery(id+"F0.wireOp",EDGE,"E3.sketch_text.stroke-50"),sQuery(id+"F0.wireOp",EDGE,"E3.sketch_text.stroke-51"),sQuery(id+"F0.wireOp",EDGE,"E3.sketch_text.stroke-52"),sQuery(id+"F0.wireOp",EDGE,"E3.sketch_text.stroke-53"),sQuery(id+"F0.wireOp",EDGE,"E8"),sQuery(id+"F0.wireOp",EDGE,"E9"),sQuery(id+"F0.wireOp",EDGE,"E10")])],"isStart":false}),makeQuery(id+"F5.opExtrude","CAP_FACE",FACE,{"disambiguationData":[OSD([sQuery(id+"F4.wireOp",EDGE,"E12.bottom"),sQuery(id+"F4.wireOp",EDGE,"E11.bottom"),sQuery(id+"F4.wireOp",EDGE,"E12.left"),sQuery(id+"F4.wireOp",EDGE,"E12.right"),sQuery(id+"F4.wireOp",EDGE,"E16"),sQuery(id+"F4.wireOp",EDGE,"E17.MirrorC")])],"isStart":false})]});
            fillet(context, id + "F9", {"entities" : qUnion([Q0]), "radius" : 5 * mm, "tangentPropagation" : true, "allowEdgeOverflow" : false});
        }
    });
